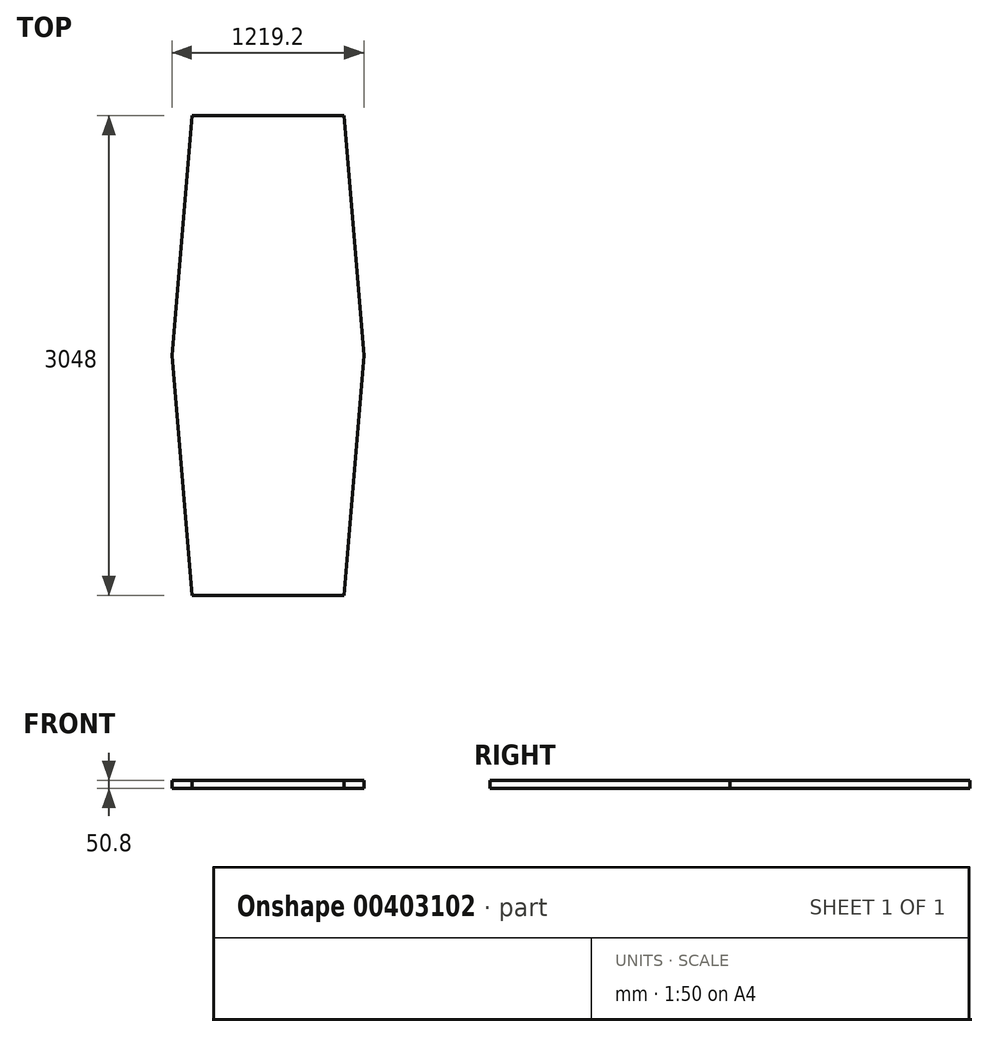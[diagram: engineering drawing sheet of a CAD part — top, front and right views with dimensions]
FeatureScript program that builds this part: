
annotation { "Feature Type Name" : "Feature", "Feature Type Description" : "" }
export const myFeature = defineFeature(function(context is Context, id is Id, definition is map)
    precondition{}
    {
        {
            var Q0;
            Q0=qCreatedBy(makeId("Top.planeOp"),FACE);
            var sketch = newSketch(context, id + "F0", { "sketchPlane" : qUnion([Q0])});
            skLineSegment(sketch, "E0", {"start": v(0, -1524) * mm, "end": v(0, 1524) * mm});
            skLineSegment(sketch, "E1", {"start": v(-482.6, 1524) * mm, "end": v(482.6, 1524) * mm});
            skLineSegment(sketch, "E2", {"start": v(482.6, 1524) * mm, "end": v(609.6, 0) * mm});
            skLineSegment(sketch, "E3", {"start": v(609.6, 0) * mm, "end": v(482.6, -1524) * mm});
            skLineSegment(sketch, "E4", {"start": v(482.6, -1524) * mm, "end": v(-482.6, -1524) * mm});
            skLineSegment(sketch, "E5", {"start": v(-482.6, -1524) * mm, "end": v(-609.6, 0) * mm});
            skLineSegment(sketch, "E6", {"start": v(-609.6, 0) * mm, "end": v(-482.6, 1524) * mm});
            skLineSegment(sketch, "E7", {"start": v(-609.6, 0) * mm, "end": v(609.6, 0) * mm});
            skSolve(sketch);
        }
        {
            var Q0;
            Q0 = qSketchRegion(id + "F0", true);
            extrude(context, id + "F1", {"entities" : qUnion([Q0]), "depth" : 50.8 * mm});
        }
    });
